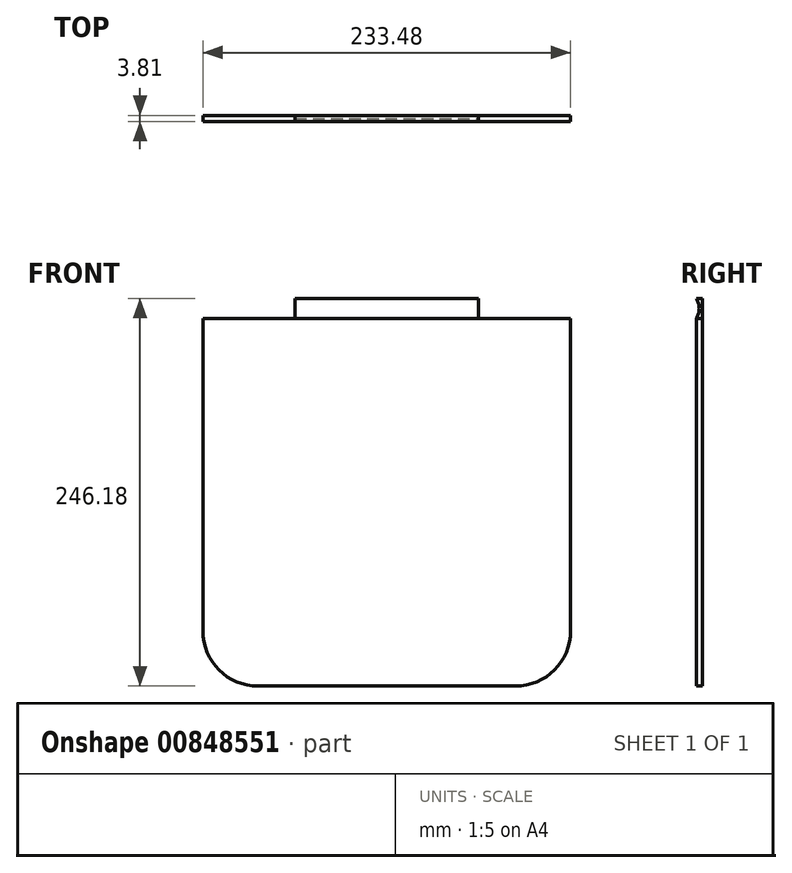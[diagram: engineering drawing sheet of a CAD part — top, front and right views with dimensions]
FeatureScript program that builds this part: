
annotation { "Feature Type Name" : "Feature", "Feature Type Description" : "" }
export const myFeature = defineFeature(function(context is Context, id is Id, definition is map)
    precondition{}
    {
        {
            var Q0;
            Q0=qCreatedBy(makeId("Front.planeOp"),FACE);
            var sketch = newSketch(context, id + "F0", { "sketchPlane" : qUnion([Q0])});
            skLineSegment(sketch, "E0.top", {"start": v(-81.74, -116.74) * mm, "end": v(81.74, -116.74) * mm});
            skLineSegment(sketch, "E0.left", {"start": v(-116.74, 116.74) * mm, "end": v(-116.74, -81.74) * mm});
            skLineSegment(sketch, "E0.right", {"start": v(116.74, 116.74) * mm, "end": v(116.74, -81.74) * mm});
            skPoint(sketch, "E0.middle", {"position": v(0, 0) * mm});
            skPoint(sketch, "E1.visualSharp", {"position": v(-116.74, -116.74) * mm});
            skArc(sketch, "E1.filletArc", {"start": v(-116.74, -81.74) * mm, "mid": v(-106.5, -106.5) * mm, "end": v(-81.74, -116.74) * mm});
            skPoint(sketch, "E2.visualSharp", {"position": v(116.74, -116.74) * mm});
            skArc(sketch, "E2.filletArc", {"start": v(81.74, -116.74) * mm, "mid": v(106.5, -106.5) * mm, "end": v(116.74, -81.74) * mm});
            skLineSegment(sketch, "E3", {"start": v(116.74, 116.74) * mm, "end": v(58.37, 116.74) * mm});
            skLineSegment(sketch, "E4", {"start": v(-116.74, 116.74) * mm, "end": v(-58.37, 116.74) * mm});
            skLineSegment(sketch, "E5", {"start": v(-58.37, 116.74) * mm, "end": v(-58.37, 129.44) * mm});
            skLineSegment(sketch, "E6", {"start": v(58.37, 116.74) * mm, "end": v(58.37, 129.44) * mm});
            skLineSegment(sketch, "E7", {"start": v(58.37, 129.44) * mm, "end": v(-58.37, 129.44) * mm});
            skSolve(sketch);
        }
        {
            var Q0;
            Q0 = qSketchRegion(id + "F0", true);
            extrude(context, id + "F1", {"entities" : qUnion([Q0]), "depth" : 3.8 * mm, "offsetDistance" : 25 * mm});
        }
        {
            var Q0;
            Q0=makeQuery(id+"F1.opExtrude","SWEPT_FACE",FACE,{"disambiguationData":[OSD([sQuery(id+"F0.wireOp",EDGE,"E6")])]});
            var sketch = newSketch(context, id + "F2", { "sketchPlane" : qUnion([Q0])});
            skArc(sketch, "E8", {"start": v(-3.8, 116.74) * mm, "mid": v(-2.08, 123.1) * mm, "end": v(-3.81, 129.44) * mm});
            skLineSegment(sketch, "E9", {"start": v(-3.81, 129.44) * mm, "end": v(-3.81, 116.74) * mm});
            skSolve(sketch);
        }
        {
            var Q0;
            Q0 = qSketchRegion(id + "F2", true);
            extrude(context, id + "F3", {"entities" : qUnion([Q0]), "operationType" : NewBodyOperationType.REMOVE, "oppositeDirection" : true, "depth" : 359 * mm, "offsetDistance" : 25 * mm});
        }
    });
